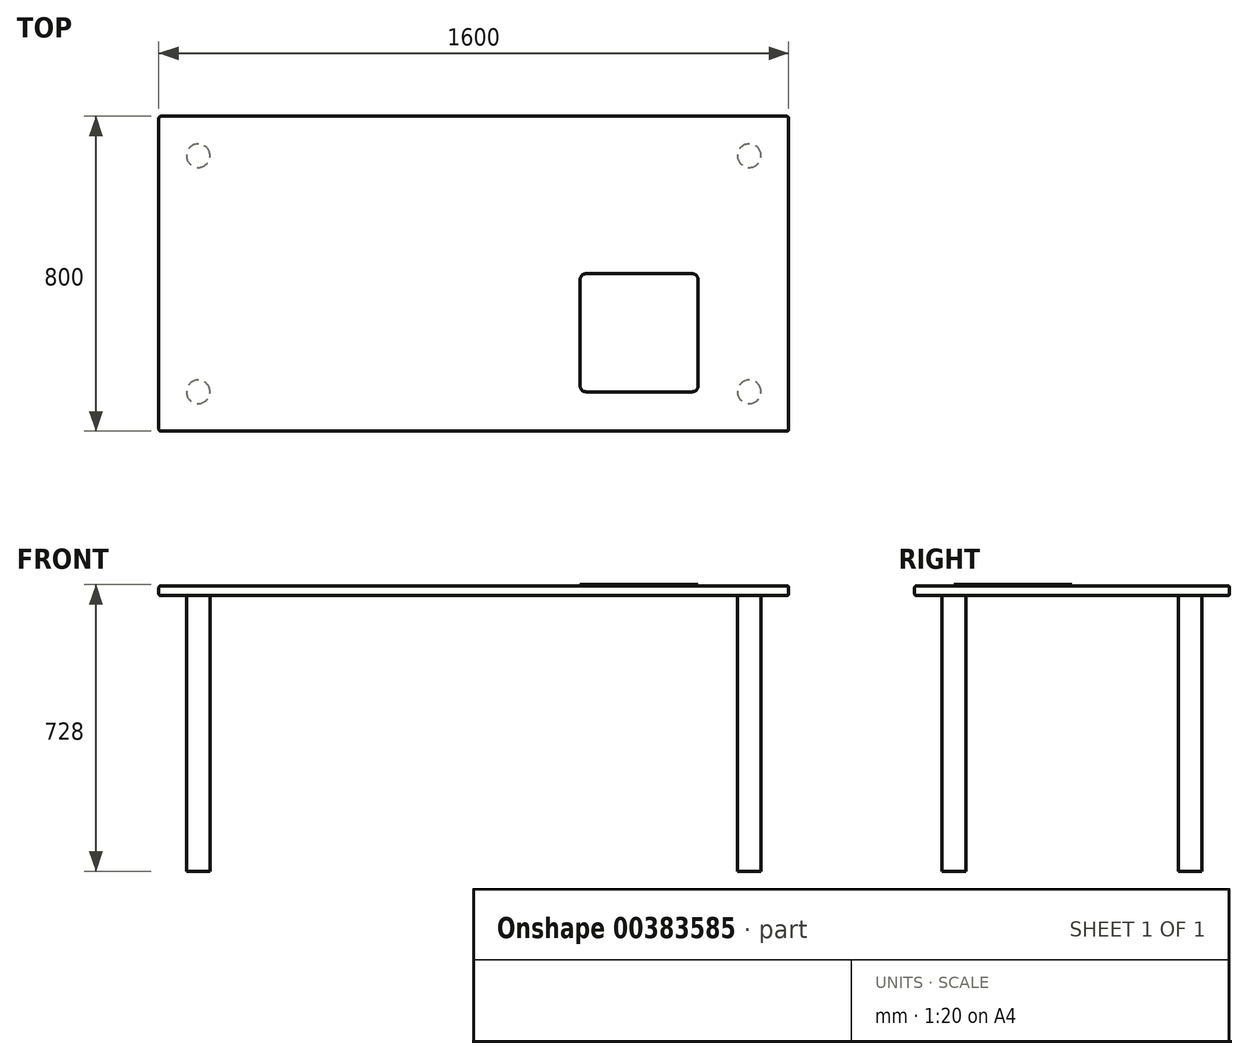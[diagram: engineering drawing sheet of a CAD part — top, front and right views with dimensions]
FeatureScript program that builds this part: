
annotation { "Feature Type Name" : "Feature", "Feature Type Description" : "" }
export const myFeature = defineFeature(function(context is Context, id is Id, definition is map)
    precondition{}
    {
        {
            var Q0;
            Q0=qCreatedBy(makeId("Top.planeOp"),FACE);
            var sketch = newSketch(context, id + "F0", { "sketchPlane" : qUnion([Q0])});
            skLineSegment(sketch, "E0.bottom", {"start": v(800, 400) * mm, "end": v(-800, 400) * mm});
            skLineSegment(sketch, "E0.top", {"start": v(800, -400) * mm, "end": v(-800, -400) * mm});
            skLineSegment(sketch, "E0.left", {"start": v(800, 400) * mm, "end": v(800, -400) * mm});
            skLineSegment(sketch, "E0.right", {"start": v(-800, 400) * mm, "end": v(-800, -400) * mm});
            skPoint(sketch, "E0.middle", {"position": v(0, 0) * mm});
            skSolve(sketch);
        }
        {
            var Q0;
            Q0=makeQuery(id+"F0.imprint","IMPRINT",FACE,{"disambiguationData":[TD([[makeQuery(id+"F0.imprint","IMPRINT",EDGE,{"derivedFrom":sQuery(id+"F0.wireOp",EDGE,"E0.bottom")}),1.0]])]});
            extrude(context, id + "F1", {"entities" : qUnion([Q0]), "depth" : 25 * mm});
        }
        {
            var Q0;
            Q0=makeQuery(id+"F1.opExtrude","CAP_EDGE",EDGE,{"disambiguationData":[OSD([sQuery(id+"F0.wireOp",EDGE,"E0.top")])],"isStart":false});
            var Q1;
            Q1=makeQuery(id+"F1.opExtrude","CAP_EDGE",EDGE,{"disambiguationData":[OSD([sQuery(id+"F0.wireOp",EDGE,"E0.top")])],"isStart":true});
            var Q2;
            Q2=makeQuery(id+"F1.opExtrude","CAP_EDGE",EDGE,{"disambiguationData":[OSD([sQuery(id+"F0.wireOp",EDGE,"E0.right")])],"isStart":false});
            var Q3;
            Q3=makeQuery(id+"F1.opExtrude","CAP_EDGE",EDGE,{"disambiguationData":[OSD([sQuery(id+"F0.wireOp",EDGE,"E0.right")])],"isStart":true});
            var Q4;
            Q4=makeQuery(id+"F1.opExtrude","CAP_EDGE",EDGE,{"disambiguationData":[OSD([sQuery(id+"F0.wireOp",EDGE,"E0.left")])],"isStart":true});
            var Q5;
            Q5=makeQuery(id+"F1.opExtrude","CAP_EDGE",EDGE,{"disambiguationData":[OSD([sQuery(id+"F0.wireOp",EDGE,"E0.left")])],"isStart":false});
            var Q6;
            Q6=makeQuery(id+"F1.opExtrude","CAP_EDGE",EDGE,{"disambiguationData":[OSD([sQuery(id+"F0.wireOp",EDGE,"E0.bottom")])],"isStart":true});
            var Q7;
            Q7=makeQuery(id+"F1.opExtrude","CAP_EDGE",EDGE,{"disambiguationData":[OSD([sQuery(id+"F0.wireOp",EDGE,"E0.bottom")])],"isStart":false});
            var Q8;
            Q8=makeQuery(id+"F1.opExtrude","SWEPT_EDGE",EDGE,{"disambiguationData":[OSD([sQuery(id+"F0.wireOp",EDGE,"E0.bottom"),sQuery(id+"F0.wireOp",EDGE,"E0.left")])]});
            var Q9;
            Q9=makeQuery(id+"F1.opExtrude","SWEPT_EDGE",EDGE,{"disambiguationData":[OSD([sQuery(id+"F0.wireOp",EDGE,"E0.top"),sQuery(id+"F0.wireOp",EDGE,"E0.left")])]});
            var Q10;
            Q10=makeQuery(id+"F1.opExtrude","SWEPT_EDGE",EDGE,{"disambiguationData":[OSD([sQuery(id+"F0.wireOp",EDGE,"E0.top"),sQuery(id+"F0.wireOp",EDGE,"E0.right")])]});
            var Q11;
            Q11=makeQuery(id+"F1.opExtrude","SWEPT_EDGE",EDGE,{"disambiguationData":[OSD([sQuery(id+"F0.wireOp",EDGE,"E0.bottom"),sQuery(id+"F0.wireOp",EDGE,"E0.right")])]});
            fillet(context, id + "F2", {"entities" : qUnion([Q0, Q1, Q2, Q3, Q4, Q5, Q6, Q7, Q8, Q9, Q10, Q11]), "radius" : 5 * mm, "tangentPropagation" : true, "allowEdgeOverflow" : false});
        }
        {
            var Q0;
            Q0=makeQuery(id+"F1.opExtrude","CAP_FACE",FACE,{"disambiguationData":[OSD([sQuery(id+"F0.wireOp",EDGE,"E0.bottom"),sQuery(id+"F0.wireOp",EDGE,"E0.top"),sQuery(id+"F0.wireOp",EDGE,"E0.left"),sQuery(id+"F0.wireOp",EDGE,"E0.right")])],"isStart":true});
            var sketch = newSketch(context, id + "F3", { "sketchPlane" : qUnion([Q0])});
            skCircle(sketch, "E1", {"center": v(-700, 300) * mm, "radius": 30 * mm});
            skCircle(sketch, "E2.0.1.0", {"center": v(-700, -300) * mm, "radius": 30 * mm});
            skCircle(sketch, "E2.1.0.0", {"center": v(700, 300) * mm, "radius": 30 * mm});
            skCircle(sketch, "E2.1.1.0", {"center": v(700, -300) * mm, "radius": 30 * mm});
            skLineSegment(sketch, "E2.direction1", {"start": v(-700, 300) * mm, "end": v(700, 300) * mm, "construction": true});
            skLineSegment(sketch, "E2.direction2", {"start": v(-700, 300) * mm, "end": v(-700, -300) * mm, "construction": true});
            skSolve(sketch);
        }
        {
            var Q0;
            Q0=makeQuery(id+"F3.imprint","IMPRINT",FACE,{"disambiguationData":[TD([[makeQuery(id+"F3.imprint","IMPRINT",EDGE,{"derivedFrom":sQuery(id+"F3.wireOp",EDGE,"E1")}),1.0]])]});
            var Q1;
            Q1=makeQuery(id+"F3.imprint","IMPRINT",FACE,{"disambiguationData":[TD([[makeQuery(id+"F3.imprint","IMPRINT",EDGE,{"derivedFrom":sQuery(id+"F3.wireOp",EDGE,"E2.1.0.0")}),1.0]])]});
            var Q2;
            Q2=makeQuery(id+"F3.imprint","IMPRINT",FACE,{"disambiguationData":[TD([[makeQuery(id+"F3.imprint","IMPRINT",EDGE,{"derivedFrom":sQuery(id+"F3.wireOp",EDGE,"E2.1.1.0")}),1.0]])]});
            var Q3;
            Q3=makeQuery(id+"F3.imprint","IMPRINT",FACE,{"disambiguationData":[TD([[makeQuery(id+"F3.imprint","IMPRINT",EDGE,{"derivedFrom":sQuery(id+"F3.wireOp",EDGE,"E2.0.1.0")}),1.0]])]});
            extrude(context, id + "F4", {"entities" : qUnion([Q0, Q1, Q2, Q3]), "depth" : 700 * mm});
        }
        {
            var Q0;
            Q0=makeQuery(id+"F1.opExtrude","CAP_FACE",FACE,{"disambiguationData":[OSD([sQuery(id+"F0.wireOp",EDGE,"E0.bottom"),sQuery(id+"F0.wireOp",EDGE,"E0.top"),sQuery(id+"F0.wireOp",EDGE,"E0.left"),sQuery(id+"F0.wireOp",EDGE,"E0.right")])],"isStart":false});
            var sketch = newSketch(context, id + "F5", { "sketchPlane" : qUnion([Q0])});
            skLineSegment(sketch, "E3.bottom", {"start": v(555, -300) * mm, "end": v(285, -300) * mm});
            skLineSegment(sketch, "E3.top", {"start": v(555, 0) * mm, "end": v(285, 0) * mm});
            skLineSegment(sketch, "E3.left", {"start": v(570, -285) * mm, "end": v(570, -15) * mm});
            skLineSegment(sketch, "E3.right", {"start": v(270, -285) * mm, "end": v(270, -15) * mm});
            skPoint(sketch, "E3.middle", {"position": v(420, -150) * mm});
            skPoint(sketch, "E4.visualSharp", {"position": v(270, 0) * mm});
            skArc(sketch, "E4.filletArc", {"start": v(285, 0) * mm, "mid": v(274.4, -4.4) * mm, "end": v(270, -15) * mm});
            skPoint(sketch, "E5.visualSharp", {"position": v(570, 0) * mm});
            skArc(sketch, "E5.filletArc", {"start": v(570, -15) * mm, "mid": v(565.6, -4.4) * mm, "end": v(555, 0) * mm});
            skPoint(sketch, "E6.visualSharp", {"position": v(570, -300) * mm});
            skArc(sketch, "E6.filletArc", {"start": v(555, -300) * mm, "mid": v(565.6, -295.6) * mm, "end": v(570, -285) * mm});
            skPoint(sketch, "E7.visualSharp", {"position": v(270, -300) * mm});
            skArc(sketch, "E7.filletArc", {"start": v(270, -285) * mm, "mid": v(274.4, -295.6) * mm, "end": v(285, -300) * mm});
            skSolve(sketch);
        }
        {
            var Q0;
            Q0=makeQuery(id+"F5.imprint","IMPRINT",FACE,{"disambiguationData":[TD([[makeQuery(id+"F5.imprint","IMPRINT",EDGE,{"derivedFrom":sQuery(id+"F5.wireOp",EDGE,"E3.bottom")}),-1.0]])]});
            extrude(context, id + "F6", {"entities" : qUnion([Q0]), "depth" : 3 * mm});
        }
    });
